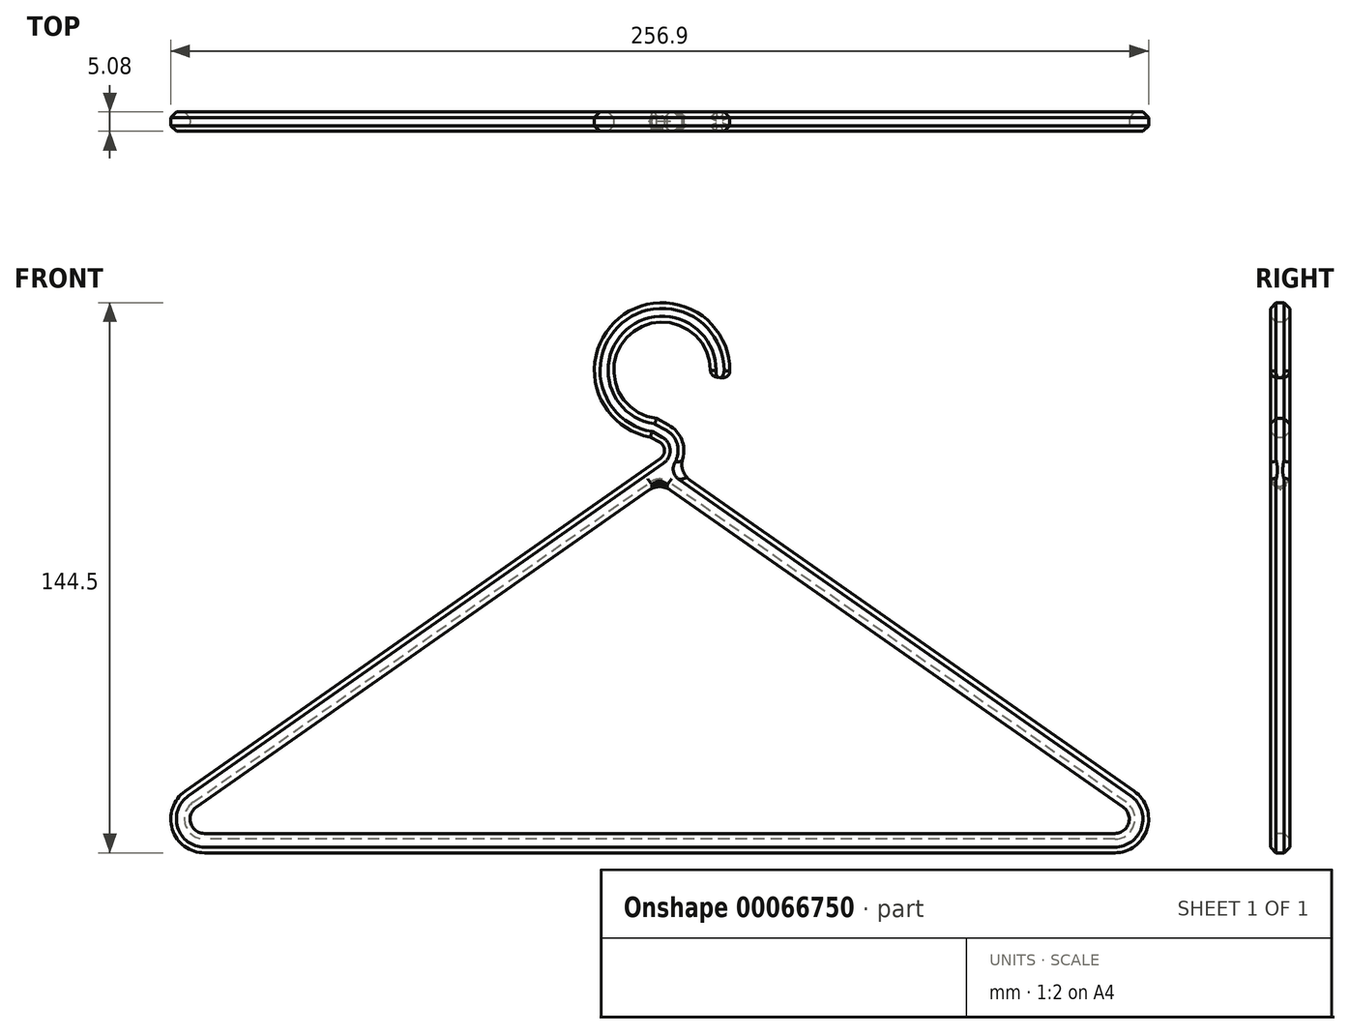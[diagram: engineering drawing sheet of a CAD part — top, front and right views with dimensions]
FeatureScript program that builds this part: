
annotation { "Feature Type Name" : "Feature", "Feature Type Description" : "" }
export const myFeature = defineFeature(function(context is Context, id is Id, definition is map)
    precondition{}
    {
        {
            var Q0;
            Q0=qCreatedBy(makeId("Front.planeOp"),FACE);
            var sketch = newSketch(context, id + "F0", { "sketchPlane" : qUnion([Q0])});
            skLineSegment(sketch, "E0", {"start": v(0, 0) * mm, "end": v(-119.56, 0) * mm});
            skLineSegment(sketch, "E1", {"start": v(-123.2, 11.55) * mm, "end": v(1.64, 98.96) * mm});
            skArc(sketch, "E2", {"start": v(15.77, 122.33) * mm, "mid": v(-8.58, 136.3) * mm, "end": v(-1.63, 109.1) * mm});
            skPoint(sketch, "E2.second.point", {"position": v(0.53, 139.42) * mm});
            skPoint(sketch, "E3.visualSharp", {"position": v(-139.7, 0) * mm});
            skArc(sketch, "E3.filletArc", {"start": v(-123.2, 11.55) * mm, "mid": v(-125.62, 4.44) * mm, "end": v(-119.56, 0) * mm});
            skLineSegment(sketch, "E4", {"start": v(-1.63, 109.1) * mm, "end": v(1.16, 107.58) * mm});
            skPoint(sketch, "E5.visualSharp", {"position": v(8.34, 103.66) * mm});
            skArc(sketch, "E5.filletArc", {"start": v(1.64, 98.96) * mm, "mid": v(3.8, 103.4) * mm, "end": v(1.16, 107.58) * mm});
            skLineSegment(sketch, "E6", {"start": v(0, 0) * mm, "end": v(119.56, 0) * mm});
            skLineSegment(sketch, "E7", {"start": v(123.2, 11.55) * mm, "end": v(0, 97.82) * mm});
            skPoint(sketch, "E8.visualSharp", {"position": v(139.7, 0) * mm});
            skArc(sketch, "E8.filletArc", {"start": v(119.56, 0) * mm, "mid": v(125.62, 4.44) * mm, "end": v(123.2, 11.55) * mm});
            skSolve(sketch);
        }
        {
            var Q0;
            Q0=qCreatedBy(makeId("Right.planeOp"),FACE);
            var sketch = newSketch(context, id + "F1", { "sketchPlane" : qUnion([Q0])});
            skCircle(sketch, "E9.cCircle", {"center": v(0, 0) * mm, "radius": 2.54 * mm, "construction": true});
            skLineSegment(sketch, "E9.0", {"start": v(-1.05, 2.54) * mm, "end": v(1.05, 2.54) * mm});
            skLineSegment(sketch, "E9.1", {"start": v(1.05, 2.54) * mm, "end": v(2.54, 1.05) * mm});
            skLineSegment(sketch, "E9.2", {"start": v(2.54, 1.05) * mm, "end": v(2.54, -1.05) * mm});
            skLineSegment(sketch, "E9.3", {"start": v(2.54, -1.05) * mm, "end": v(1.05, -2.54) * mm});
            skLineSegment(sketch, "E9.4", {"start": v(1.05, -2.54) * mm, "end": v(-1.05, -2.54) * mm});
            skLineSegment(sketch, "E9.5", {"start": v(-1.05, -2.54) * mm, "end": v(-2.54, -1.05) * mm});
            skLineSegment(sketch, "E9.6", {"start": v(-2.54, -1.05) * mm, "end": v(-2.54, 1.05) * mm});
            skLineSegment(sketch, "E9.7", {"start": v(-2.54, 1.05) * mm, "end": v(-1.05, 2.54) * mm});
            skPoint(sketch, "E9.0.midPoint", {"position": v(0, 2.54) * mm});
            skSolve(sketch);
        }
        {
            var Q0;
            Q0=makeQuery(id+"F1.imprint","IMPRINT",FACE,{"disambiguationData":[TD([[makeQuery(id+"F1.imprint","IMPRINT",EDGE,{"derivedFrom":sQuery(id+"F1.wireOp",EDGE,"E9.0")}),-1.0]])]});
            var Q1;
            Q1=sQuery(id+"F0.wireOp",EDGE,"E0");
            var Q2;
            Q2=sQuery(id+"F0.wireOp",EDGE,"E1");
            var Q3;
            Q3=sQuery(id+"F0.wireOp",EDGE,"E3.filletArc");
            var Q4;
            Q4=sQuery(id+"F0.wireOp",EDGE,"E5.filletArc");
            var Q5;
            Q5=sQuery(id+"F0.wireOp",EDGE,"E4");
            var Q6;
            Q6=sQuery(id+"F0.wireOp",EDGE,"E2");
            sweep(context, id + "F2", {"profiles" : qUnion([Q0]), "path" : qUnion([Q1, Q2, Q3, Q4, Q5, Q6])});
        }
        {
            var Q0;
            Q0=makeQuery(id+"F2.opSweep","SWEPT_BODY",BODY,{"disambiguationData":[OSD([sQuery(id+"F0.wireOp",EDGE,"E0"),sQuery(id+"F1.wireOp",EDGE,"E9.0"),sQuery(id+"F1.wireOp",EDGE,"E9.1"),sQuery(id+"F1.wireOp",EDGE,"E9.2"),sQuery(id+"F1.wireOp",EDGE,"E9.3"),sQuery(id+"F1.wireOp",EDGE,"E9.4"),sQuery(id+"F1.wireOp",EDGE,"E9.5"),sQuery(id+"F1.wireOp",EDGE,"E9.6"),sQuery(id+"F1.wireOp",EDGE,"E9.7")])]});
            var Q1;
            Q1=qCreatedBy(makeId("Front.planeOp"),FACE);
            mirror(context, id + "F3", {"operationType" : NewBodyOperationType.ADD, "entities" : qUnion([Q0]), "mirrorPlane" : qUnion([Q1])});
        }
        {
            var Q0;
            Q0 = qSketchRegion(id + "F1", true);
            var Q1;
            Q1=sQuery(id+"F0.wireOp",EDGE,"E6");
            var Q2;
            Q2=sQuery(id+"F0.wireOp",EDGE,"E7");
            var Q3;
            Q3=sQuery(id+"F0.wireOp",EDGE,"E8.filletArc");
            sweep(context, id + "F4", {"operationType" : NewBodyOperationType.ADD, "profiles" : qUnion([Q0]), "path" : qUnion([Q1, Q2, Q3])});
        }
        {
            var Q0;
            Q0=makeQuery(id+"F4.boolean.opBoolean","INTERSECT",EDGE,{"derivedFrom":[makeQuery(id+"F2.opSweep","SWEPT_FACE",FACE,{"disambiguationData":[OSD([sQuery(id+"F0.wireOp",EDGE,"E5.filletArc"),sQuery(id+"F1.wireOp",EDGE,"E9.7")])]}),makeQuery(id+"F4.opSweep","SWEPT_FACE",FACE,{"disambiguationData":[OSD([sQuery(id+"F0.wireOp",EDGE,"E7"),sQuery(id+"F1.wireOp",EDGE,"E9.5")])]})]});
            var Q1;
            Q1=makeQuery(id+"F4.boolean.opBoolean","INTERSECT",EDGE,{"derivedFrom":[makeQuery(id+"F2.opSweep","SWEPT_FACE",FACE,{"disambiguationData":[OSD([sQuery(id+"F0.wireOp",EDGE,"E5.filletArc"),sQuery(id+"F1.wireOp",EDGE,"E9.0")])]}),makeQuery(id+"F4.opSweep","SWEPT_FACE",FACE,{"disambiguationData":[OSD([sQuery(id+"F0.wireOp",EDGE,"E7"),sQuery(id+"F1.wireOp",EDGE,"E9.4")])]})]});
            var Q2;
            Q2=makeQuery(id+"F4.boolean.opBoolean","INTERSECT",EDGE,{"derivedFrom":[makeQuery(id+"F2.opSweep","SWEPT_FACE",FACE,{"disambiguationData":[OSD([sQuery(id+"F0.wireOp",EDGE,"E5.filletArc"),sQuery(id+"F1.wireOp",EDGE,"E9.1")])]}),makeQuery(id+"F4.opSweep","SWEPT_FACE",FACE,{"disambiguationData":[OSD([sQuery(id+"F0.wireOp",EDGE,"E7"),sQuery(id+"F1.wireOp",EDGE,"E9.3")])]})]});
            var Q3;
            {var subQ0=sQuery(id+"F1.wireOp",EDGE,"E9.0");Q3=makeQuery(id+"F4.boolean.opBoolean","INTERSECT",EDGE,{"derivedFrom":[makeQuery(id+"F2.opSweep","SWEPT_FACE",FACE,{"disambiguationData":[OSD([sQuery(id+"F0.wireOp",EDGE,"E1"),subQ0])]}),makeQuery(id+"F4.opSweep","SWEPT_FACE",FACE,{"disambiguationData":[OSD([sQuery(id+"F0.wireOp",EDGE,"E7"),subQ0])]})]});}
            var Q4;
            {var subQ0=sQuery(id+"F1.wireOp",EDGE,"E9.7");Q4=makeQuery(id+"F4.boolean.opBoolean","INTERSECT",EDGE,{"derivedFrom":[makeQuery(id+"F2.opSweep","SWEPT_FACE",FACE,{"disambiguationData":[OSD([sQuery(id+"F0.wireOp",EDGE,"E1"),subQ0])]}),makeQuery(id+"F4.opSweep","SWEPT_FACE",FACE,{"disambiguationData":[OSD([sQuery(id+"F0.wireOp",EDGE,"E7"),subQ0])]})]});}
            var Q5;
            {var subQ0=sQuery(id+"F1.wireOp",EDGE,"E9.1");Q5=makeQuery(id+"F4.boolean.opBoolean","INTERSECT",EDGE,{"derivedFrom":[makeQuery(id+"F2.opSweep","SWEPT_FACE",FACE,{"disambiguationData":[OSD([sQuery(id+"F0.wireOp",EDGE,"E1"),subQ0])]}),makeQuery(id+"F4.opSweep","SWEPT_FACE",FACE,{"disambiguationData":[OSD([sQuery(id+"F0.wireOp",EDGE,"E7"),subQ0])]})]});}
            fillet(context, id + "F5", {"entities" : qUnion([Q0, Q1, Q2, Q3, Q4, Q5]), "radius" : 5.08 * mm, "tangentPropagation" : true, "allowEdgeOverflow" : false});
        }
        {
            var Q0;
            {var subQ0=sQuery(id+"F1.wireOp",EDGE,"E9.7");var subQ1=sQuery(id+"F1.wireOp",EDGE,"E9.0");Q0=makeQuery(id+"F4.boolean.opBoolean","MERGE",EDGE,{"derivedFrom":[makeQuery(id+"F2.opSweep","SWEPT_EDGE",EDGE,{"disambiguationData":[OSD([sQuery(id+"F0.wireOp",EDGE,"E0"),subQ1,subQ0])]}),makeQuery(id+"F4.opSweep","SWEPT_EDGE",EDGE,{"disambiguationData":[OSD([sQuery(id+"F0.wireOp",EDGE,"E6"),subQ1,subQ0])]})]});}
            var Q1;
            {var subQ0=sQuery(id+"F1.wireOp",EDGE,"E9.7");var subQ1=sQuery(id+"F1.wireOp",EDGE,"E9.6");Q1=makeQuery(id+"F4.boolean.opBoolean","MERGE",EDGE,{"derivedFrom":[makeQuery(id+"F2.opSweep","SWEPT_EDGE",EDGE,{"disambiguationData":[OSD([sQuery(id+"F0.wireOp",EDGE,"E0"),subQ1,subQ0])]}),makeQuery(id+"F4.opSweep","SWEPT_EDGE",EDGE,{"disambiguationData":[OSD([sQuery(id+"F0.wireOp",EDGE,"E6"),subQ1,subQ0])]})]});}
            var Q2;
            {var subQ0=sQuery(id+"F1.wireOp",EDGE,"E9.1");var subQ1=sQuery(id+"F1.wireOp",EDGE,"E9.0");Q2=makeQuery(id+"F4.boolean.opBoolean","MERGE",EDGE,{"derivedFrom":[makeQuery(id+"F2.opSweep","SWEPT_EDGE",EDGE,{"disambiguationData":[OSD([sQuery(id+"F0.wireOp",EDGE,"E0"),subQ1,subQ0])]}),makeQuery(id+"F4.opSweep","SWEPT_EDGE",EDGE,{"disambiguationData":[OSD([sQuery(id+"F0.wireOp",EDGE,"E6"),subQ1,subQ0])]})]});}
            fillet(context, id + "F6", {"entities" : qUnion([Q0, Q1, Q2]), "radius" : 2.54 * mm, "tangentPropagation" : true, "allowEdgeOverflow" : false});
        }
        {
            var Q0;
            Q0=makeQuery(id+"F2.opSweep","CAP_EDGE",EDGE,{"disambiguationData":[OSD([sQuery(id+"F0.wireOp",VERTEX,"E2.start"),sQuery(id+"F1.wireOp",EDGE,"E9.7")])],"isStart":false});
            var Q1;
            Q1=makeQuery(id+"F2.opSweep","CAP_EDGE",EDGE,{"disambiguationData":[OSD([sQuery(id+"F0.wireOp",VERTEX,"E2.start"),sQuery(id+"F1.wireOp",EDGE,"E9.3")])],"isStart":false});
            var Q2;
            Q2=makeQuery(id+"F2.opSweep","CAP_EDGE",EDGE,{"disambiguationData":[OSD([sQuery(id+"F0.wireOp",VERTEX,"E2.start"),sQuery(id+"F1.wireOp",EDGE,"E9.5")])],"isStart":false});
            var Q3;
            Q3=makeQuery(id+"F2.opSweep","CAP_EDGE",EDGE,{"disambiguationData":[OSD([sQuery(id+"F0.wireOp",VERTEX,"E2.start"),sQuery(id+"F1.wireOp",EDGE,"E9.4")])],"isStart":false});
            var Q4;
            Q4=makeQuery(id+"F2.opSweep","CAP_EDGE",EDGE,{"disambiguationData":[OSD([sQuery(id+"F0.wireOp",VERTEX,"E2.start"),sQuery(id+"F1.wireOp",EDGE,"E9.0")])],"isStart":false});
            var Q5;
            Q5=makeQuery(id+"F2.opSweep","CAP_EDGE",EDGE,{"disambiguationData":[OSD([sQuery(id+"F0.wireOp",VERTEX,"E2.start"),sQuery(id+"F1.wireOp",EDGE,"E9.1")])],"isStart":false});
            var Q6;
            Q6=makeQuery(id+"F2.opSweep","CAP_EDGE",EDGE,{"disambiguationData":[OSD([sQuery(id+"F0.wireOp",VERTEX,"E2.start"),sQuery(id+"F1.wireOp",EDGE,"E9.2")])],"isStart":false});
            var Q7;
            Q7=makeQuery(id+"F2.opSweep","CAP_EDGE",EDGE,{"disambiguationData":[OSD([sQuery(id+"F0.wireOp",VERTEX,"E2.start"),sQuery(id+"F1.wireOp",EDGE,"E9.6")])],"isStart":false});
            fillet(context, id + "F7", {"entities" : qUnion([Q0, Q1, Q2, Q3, Q4, Q5, Q6, Q7]), "radius" : 1.78 * mm, "tangentPropagation" : true, "allowEdgeOverflow" : false});
        }
    });
